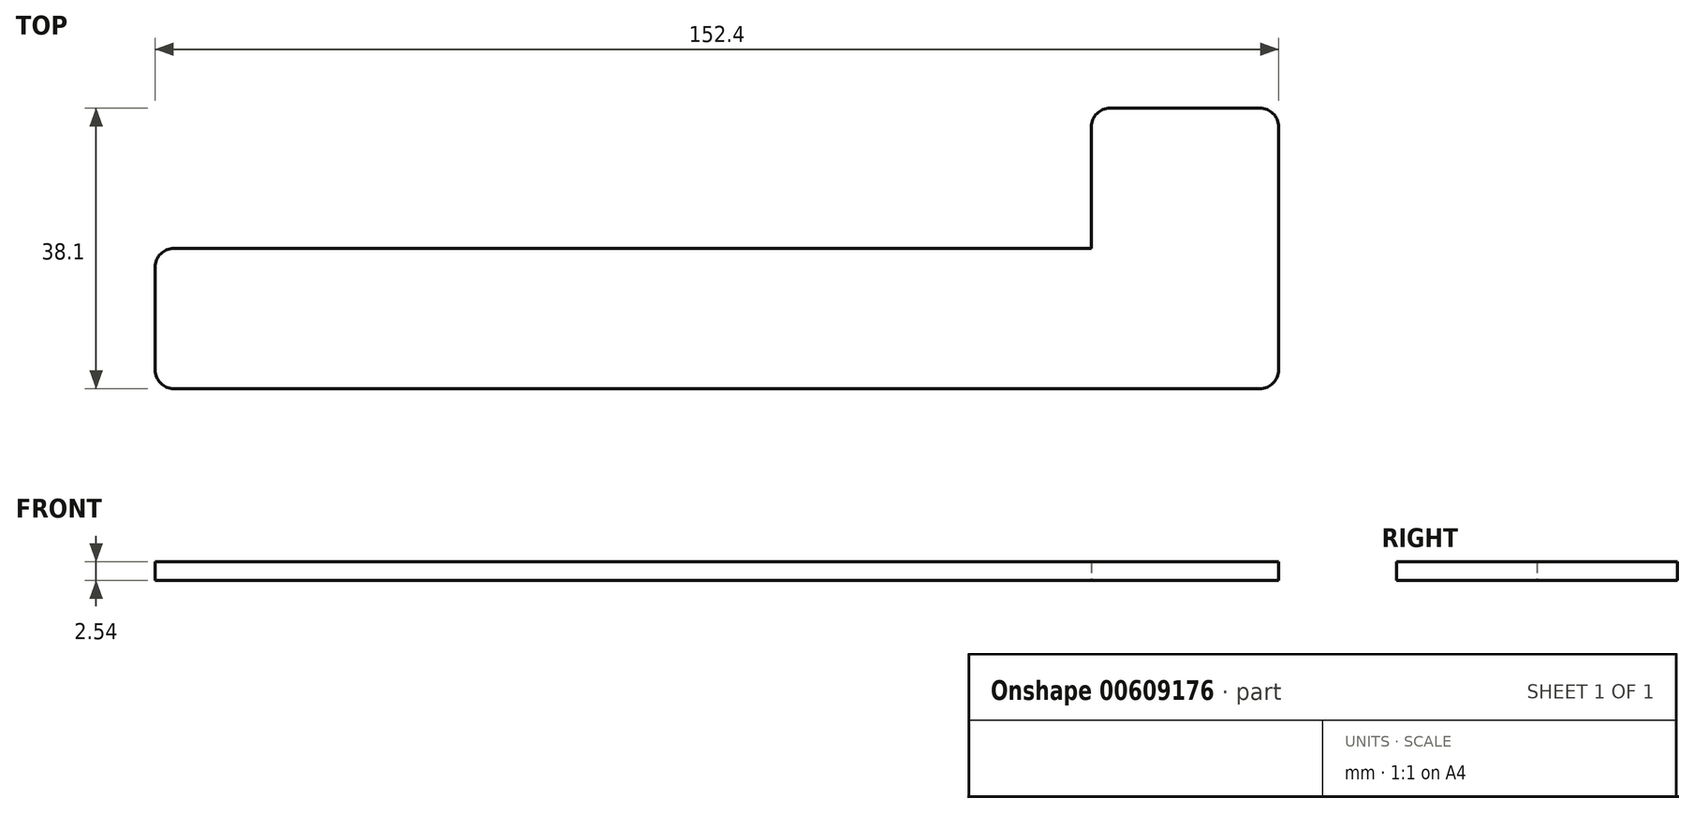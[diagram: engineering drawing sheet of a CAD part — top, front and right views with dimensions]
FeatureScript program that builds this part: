
annotation { "Feature Type Name" : "Feature", "Feature Type Description" : "" }
export const myFeature = defineFeature(function(context is Context, id is Id, definition is map)
    precondition{}
    {
        {
            var Q0;
            Q0=qCreatedBy(makeId("Top.planeOp"),FACE);
            var sketch = newSketch(context, id + "F0", { "sketchPlane" : qUnion([Q0])});
            skLineSegment(sketch, "E0.bottom", {"start": v(-72.4, 2.61) * mm, "end": v(52.06, 2.61) * mm});
            skLineSegment(sketch, "E0.top", {"start": v(-72.4, -16.44) * mm, "end": v(74.92, -16.44) * mm});
            skLineSegment(sketch, "E0.left", {"start": v(-74.94, 0.07) * mm, "end": v(-74.94, -13.9) * mm});
            skLineSegment(sketch, "E0.right", {"start": v(77.46, 2.61) * mm, "end": v(77.46, -13.9) * mm});
            skLineSegment(sketch, "E1", {"start": v(52.06, 2.61) * mm, "end": v(52.06, 19.12) * mm});
            skLineSegment(sketch, "E2", {"start": v(54.6, 21.66) * mm, "end": v(74.92, 21.66) * mm});
            skLineSegment(sketch, "E3", {"start": v(77.46, 2.61) * mm, "end": v(77.46, 19.12) * mm});
            skPoint(sketch, "E4.visualSharp", {"position": v(-74.94, 2.61) * mm});
            skArc(sketch, "E4.filletArc", {"start": v(-72.4, 2.61) * mm, "mid": v(-74.2, 1.87) * mm, "end": v(-74.94, 0.07) * mm});
            skPoint(sketch, "E5.visualSharp", {"position": v(-74.94, -16.44) * mm});
            skArc(sketch, "E5.filletArc", {"start": v(-74.94, -13.9) * mm, "mid": v(-74.2, -15.7) * mm, "end": v(-72.4, -16.44) * mm});
            skPoint(sketch, "E6.visualSharp", {"position": v(77.46, -16.44) * mm});
            skArc(sketch, "E6.filletArc", {"start": v(74.92, -16.44) * mm, "mid": v(76.71, -15.7) * mm, "end": v(77.46, -13.9) * mm});
            skPoint(sketch, "E7.visualSharp", {"position": v(52.06, 21.66) * mm});
            skArc(sketch, "E7.filletArc", {"start": v(54.6, 21.66) * mm, "mid": v(52.8, 20.92) * mm, "end": v(52.06, 19.12) * mm});
            skPoint(sketch, "E8.visualSharp", {"position": v(77.46, 21.66) * mm});
            skArc(sketch, "E8.filletArc", {"start": v(77.46, 19.12) * mm, "mid": v(76.71, 20.92) * mm, "end": v(74.92, 21.66) * mm});
            skSolve(sketch);
        }
        {
            var Q0;
            Q0=makeQuery(id+"F0.imprint","IMPRINT",FACE,{"disambiguationData":[TD([[makeQuery(id+"F0.imprint","IMPRINT",EDGE,{"derivedFrom":sQuery(id+"F0.wireOp",EDGE,"E0.bottom")}),-1.0]])]});
            extrude(context, id + "F1", {"entities" : qUnion([Q0]), "depth" : 2.54 * mm, "offsetDistance" : 25.4 * mm});
        }
    });
